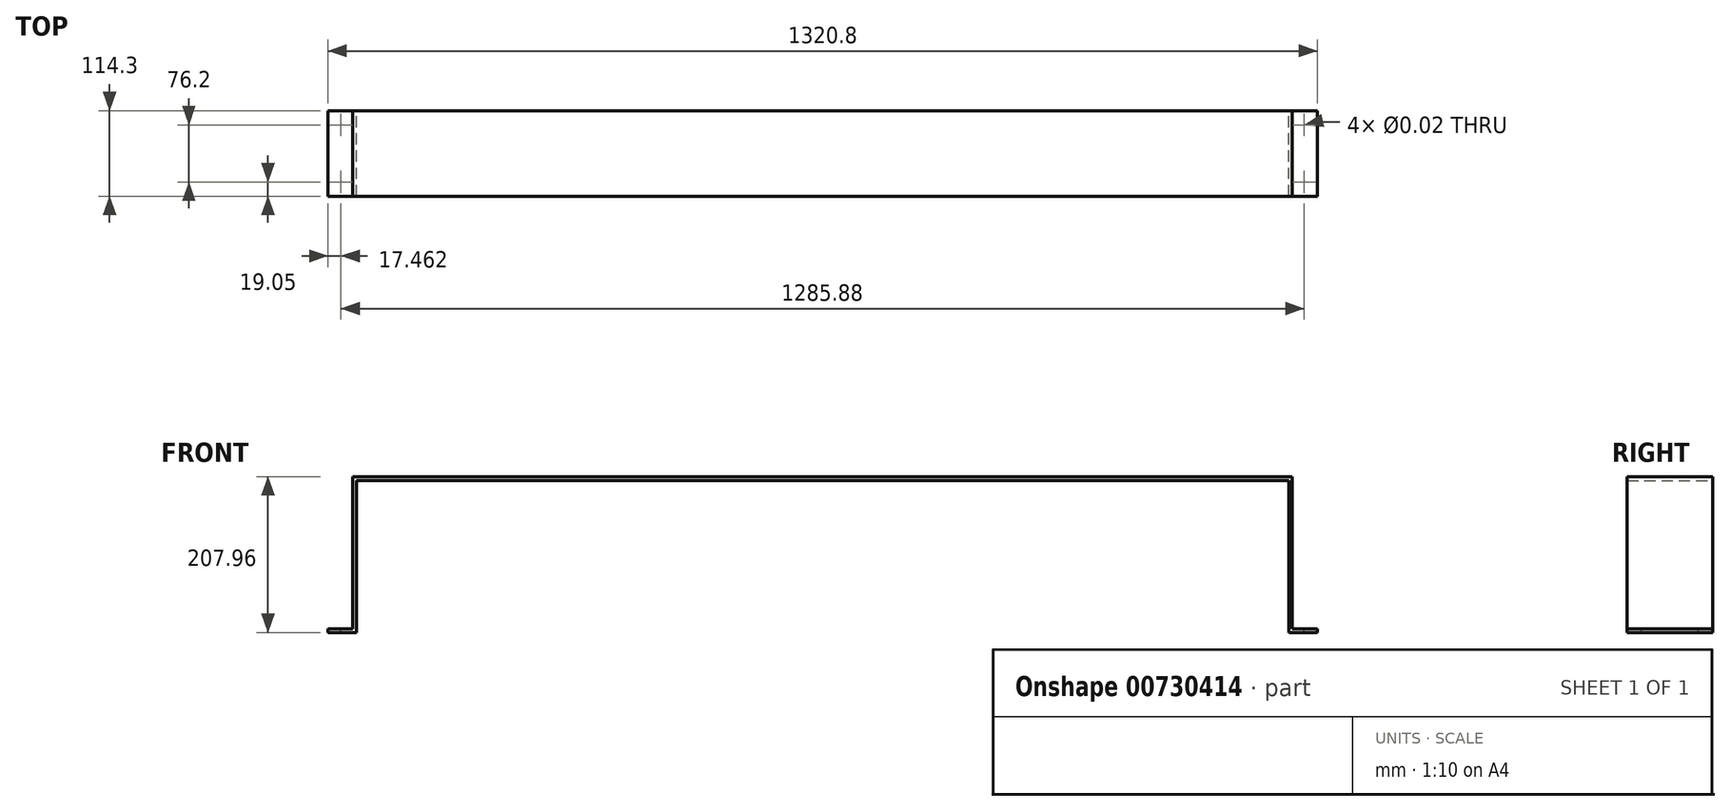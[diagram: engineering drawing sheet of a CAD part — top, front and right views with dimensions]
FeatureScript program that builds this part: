
annotation { "Feature Type Name" : "Feature", "Feature Type Description" : "" }
export const myFeature = defineFeature(function(context is Context, id is Id, definition is map)
    precondition{}
    {
        {
            var Q0;
            Q0=qCreatedBy(makeId("Front.planeOp"),FACE);
            var sketch = newSketch(context, id + "F0", { "sketchPlane" : qUnion([Q0])});
            skLineSegment(sketch, "E0", {"start": v(-660.4, 4.76) * mm, "end": v(-627.06, 4.76) * mm});
            skLineSegment(sketch, "E1", {"start": v(-627.06, 4.76) * mm, "end": v(-627.06, 207.96) * mm});
            skLineSegment(sketch, "E2", {"start": v(-627.06, 207.96) * mm, "end": v(627.06, 207.96) * mm});
            skLineSegment(sketch, "E3", {"start": v(627.06, 207.96) * mm, "end": v(627.06, 4.76) * mm});
            skLineSegment(sketch, "E4", {"start": v(627.06, 4.76) * mm, "end": v(660.4, 4.76) * mm});
            skLineSegment(sketch, "E5", {"start": v(660.4, 4.76) * mm, "end": v(660.4, 0) * mm});
            skLineSegment(sketch, "E6", {"start": v(-660.4, 0) * mm, "end": v(-660.4, 4.76) * mm});
            skLineSegment(sketch, "E7", {"start": v(-660.4, 0) * mm, "end": v(-622.3, 0) * mm});
            skLineSegment(sketch, "E8", {"start": v(-622.3, 0) * mm, "end": v(-622.3, 203.2) * mm});
            skLineSegment(sketch, "E9", {"start": v(-622.3, 203.2) * mm, "end": v(622.3, 203.2) * mm});
            skLineSegment(sketch, "E10", {"start": v(622.3, 203.2) * mm, "end": v(622.3, 0) * mm});
            skLineSegment(sketch, "E11", {"start": v(622.3, 0) * mm, "end": v(660.4, 0) * mm});
            skSolve(sketch);
        }
        {
            var Q0;
            Q0 = qSketchRegion(id + "F0", true);
            extrude(context, id + "F1", {"entities" : qUnion([Q0]), "endBound" : BoundingType.SYMMETRIC, "depth" : 114.3 * mm, "offsetDistance" : 25.4 * mm});
        }
        {
            var Q0;
            Q0=makeQuery(id+"F1.opExtrude","SWEPT_FACE",FACE,{"disambiguationData":[OSD([sQuery(id+"F0.wireOp",EDGE,"E0")])]});
            var sketch = newSketch(context, id + "F2", { "sketchPlane" : qUnion([Q0])});
            skPoint(sketch, "E12", {"position": v(-642.94, 38.1) * mm});
            skPoint(sketch, "E13", {"position": v(-642.94, -38.1) * mm});
            skPoint(sketch, "E14", {"position": v(642.94, 38.1) * mm});
            skPoint(sketch, "E15", {"position": v(642.94, -38.1) * mm});
            skSolve(sketch);
        }
        {
            var Q0;
            Q0=sQuery(id+"F2.wireOp",VERTEX,"E12");
            var Q1;
            Q1=sQuery(id+"F2.wireOp",VERTEX,"E13");
            var Q2;
            Q2=sQuery(id+"F2.wireOp",VERTEX,"E14");
            var Q3;
            Q3=sQuery(id+"F2.wireOp",VERTEX,"E15");
            var Q4;
            Q4=makeQuery(id+"F1.opExtrude","SWEPT_BODY",BODY,{"disambiguationData":[OSD([sQuery(id+"F0.wireOp",EDGE,"E0"),sQuery(id+"F0.wireOp",EDGE,"E1"),sQuery(id+"F0.wireOp",EDGE,"E2"),sQuery(id+"F0.wireOp",EDGE,"E3"),sQuery(id+"F0.wireOp",EDGE,"E4"),sQuery(id+"F0.wireOp",EDGE,"E5"),sQuery(id+"F0.wireOp",EDGE,"E6"),sQuery(id+"F0.wireOp",EDGE,"E7"),sQuery(id+"F0.wireOp",EDGE,"E8"),sQuery(id+"F0.wireOp",EDGE,"E9"),sQuery(id+"F0.wireOp",EDGE,"E10"),sQuery(id+"F0.wireOp",EDGE,"E11")])]});
            hole(context, id + "F3", {"style" : HoleStyle.SIMPLE, "endStyle" : HoleEndStyle.THROUGH, "standardTappedOrClearance" : lookupTablePath({ "standard" : "ANSI", "size" : "1/2 (0.5)", "type" : "Drilled" }), "standardBlindInLast" : lookupTablePath({ "standard" : "ANSI", "size" : "1/2", "type" : "Drilled" }), "holeDiameter" : 1 / 50.8 * mm, "majorDiameter" : 6.35 * mm, "isTappedThrough" : true, "tappedDepth" : 6 * mm, "tapClearance" : 3, "startFromSketch" : true, "locations" : qUnion([Q0, Q1, Q2, Q3]), "scope" : qUnion([Q4])});
        }
    });
